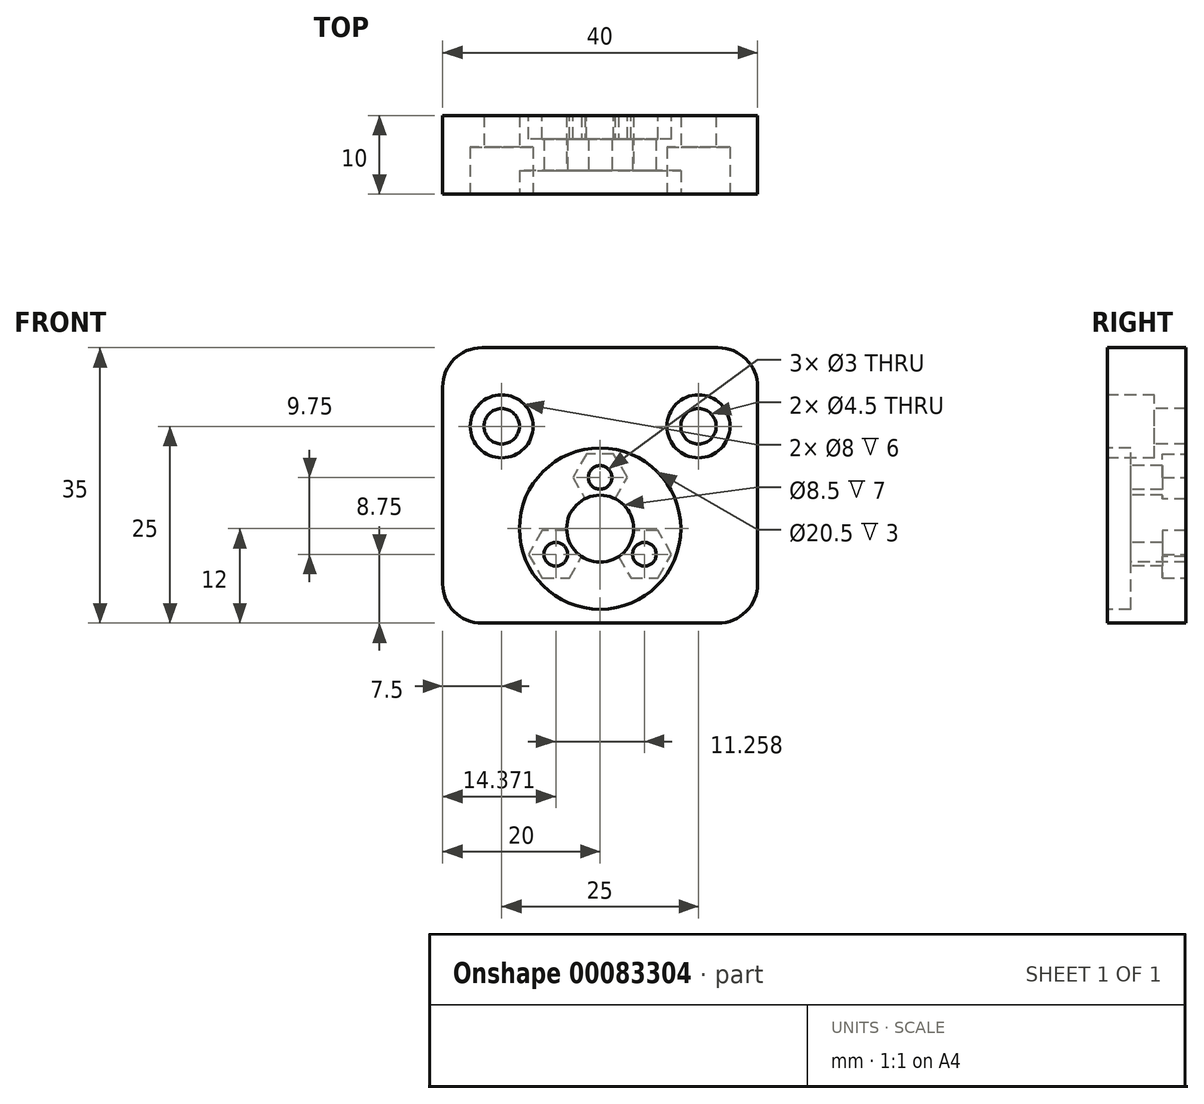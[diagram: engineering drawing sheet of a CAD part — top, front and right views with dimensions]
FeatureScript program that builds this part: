
annotation { "Feature Type Name" : "Feature", "Feature Type Description" : "" }
export const myFeature = defineFeature(function(context is Context, id is Id, definition is map)
    precondition{}
    {
        {
            var Q0;
            Q0=qCreatedBy(makeId("Front.planeOp"),FACE);
            var sketch = newSketch(context, id + "F0", { "sketchPlane" : qUnion([Q0])});
            skLineSegment(sketch, "E0.bottom", {"start": v(-20, -12) * mm, "end": v(20, -12) * mm});
            skLineSegment(sketch, "E0.top", {"start": v(-20, 23) * mm, "end": v(20, 23) * mm});
            skLineSegment(sketch, "E0.left", {"start": v(-20, -12) * mm, "end": v(-20, 23) * mm});
            skLineSegment(sketch, "E0.right", {"start": v(20, -12) * mm, "end": v(20, 23) * mm});
            skCircle(sketch, "E1", {"center": v(0, 0) * mm, "radius": 4.25 * mm});
            skCircle(sketch, "E2.cCircle", {"center": v(0, 0) * mm, "radius": 6.5 * mm, "construction": true});
            skLineSegment(sketch, "E2.0", {"start": v(0, 6.5) * mm, "end": v(5.63, -3.25) * mm, "construction": true});
            skLineSegment(sketch, "E2.1", {"start": v(5.63, -3.25) * mm, "end": v(-5.63, -3.25) * mm, "construction": true});
            skLineSegment(sketch, "E2.2", {"start": v(-5.63, -3.25) * mm, "end": v(0, 6.5) * mm, "construction": true});
            skCircle(sketch, "E3", {"center": v(0, 0) * mm, "radius": 10.25 * mm});
            skCircle(sketch, "E4", {"center": v(0, 6.5) * mm, "radius": 1.5 * mm});
            skCircle(sketch, "E5", {"center": v(5.63, -3.25) * mm, "radius": 1.5 * mm});
            skCircle(sketch, "E6", {"center": v(-5.63, -3.25) * mm, "radius": 1.5 * mm});
            skLineSegment(sketch, "E7", {"start": v(0, -14.58) * mm, "end": v(0, 17.23) * mm, "construction": true});
            skLineSegment(sketch, "E8", {"start": v(-16.58, 0) * mm, "end": v(25.82, 0) * mm, "construction": true});
            skCircle(sketch, "E9", {"center": v(-12.5, 13) * mm, "radius": 2.25 * mm});
            skCircle(sketch, "E10", {"center": v(12.5, 13) * mm, "radius": 2.25 * mm});
            skCircle(sketch, "E11", {"center": v(-12.5, 13) * mm, "radius": 4 * mm});
            skCircle(sketch, "E12", {"center": v(12.5, 13) * mm, "radius": 4 * mm});
            skSolve(sketch);
        }
        {
            var Q0;
            Q0=makeQuery(id+"F0.imprint","IMPRINT",FACE,{"disambiguationData":[TD([[makeQuery(id+"F0.imprint","IMPRINT",EDGE,{"derivedFrom":sQuery(id+"F0.wireOp",EDGE,"E0.bottom")}),1.0]])]});
            var Q1;
            Q1=makeQuery(id+"F0.imprint","IMPRINT",FACE,{"disambiguationData":[TD([[makeQuery(id+"F0.imprint","IMPRINT",EDGE,{"derivedFrom":sQuery(id+"F0.wireOp",EDGE,"E9")}),-1.0]])]});
            var Q2;
            Q2=makeQuery(id+"F0.imprint","IMPRINT",FACE,{"disambiguationData":[TD([[makeQuery(id+"F0.imprint","IMPRINT",EDGE,{"derivedFrom":sQuery(id+"F0.wireOp",EDGE,"E10")}),-1.0]])]});
            var Q3;
            Q3=makeQuery(id+"F0.imprint","IMPRINT",FACE,{"disambiguationData":[TD([[makeQuery(id+"F0.imprint","IMPRINT",EDGE,{"derivedFrom":sQuery(id+"F0.wireOp",EDGE,"E1")}),-1.0]])]});
            extrude(context, id + "F1", {"entities" : qUnion([Q0, Q1, Q2, Q3]), "oppositeDirection" : true, "depth" : 10 * mm});
        }
        {
            var Q0;
            Q0=makeQuery(id+"F0.imprint","IMPRINT",FACE,{"disambiguationData":[TD([[makeQuery(id+"F0.imprint","IMPRINT",EDGE,{"derivedFrom":sQuery(id+"F0.wireOp",EDGE,"E10")}),-1.0]])]});
            var Q1;
            Q1=makeQuery(id+"F0.imprint","IMPRINT",FACE,{"disambiguationData":[TD([[makeQuery(id+"F0.imprint","IMPRINT",EDGE,{"derivedFrom":sQuery(id+"F0.wireOp",EDGE,"E9")}),-1.0]])]});
            extrude(context, id + "F2", {"entities" : qUnion([Q0, Q1]), "operationType" : NewBodyOperationType.REMOVE, "oppositeDirection" : true, "depth" : 6 * mm});
        }
        {
            var Q0;
            Q0=makeQuery(id+"F0.imprint","IMPRINT",FACE,{"disambiguationData":[TD([[makeQuery(id+"F0.imprint","IMPRINT",EDGE,{"derivedFrom":sQuery(id+"F0.wireOp",EDGE,"E1")}),-1.0]])]});
            extrude(context, id + "F3", {"entities" : qUnion([Q0]), "operationType" : NewBodyOperationType.REMOVE, "oppositeDirection" : true, "depth" : 3 * mm});
        }
        {
            var Q0;
            Q0=makeQuery(id+"F1.opExtrude","CAP_FACE",FACE,{"disambiguationData":[OSD([sQuery(id+"F0.wireOp",EDGE,"E0.bottom"),sQuery(id+"F0.wireOp",EDGE,"E0.top"),sQuery(id+"F0.wireOp",EDGE,"E0.left"),sQuery(id+"F0.wireOp",EDGE,"E0.right"),sQuery(id+"F0.wireOp",EDGE,"E1"),sQuery(id+"F0.wireOp",EDGE,"E4"),sQuery(id+"F0.wireOp",EDGE,"E5"),sQuery(id+"F0.wireOp",EDGE,"E6"),sQuery(id+"F0.wireOp",EDGE,"E9"),sQuery(id+"F0.wireOp",EDGE,"E10")])],"isStart":false});
            var sketch = newSketch(context, id + "F4", { "sketchPlane" : qUnion([Q0])});
            skCircle(sketch, "E13", {"center": v(0, 0) * mm, "radius": 3.5 * mm, "construction": true});
            skCircle(sketch, "E14.cCircle", {"center": v(0, 6.5) * mm, "radius": 3 * mm, "construction": true});
            skLineSegment(sketch, "E14.0", {"start": v(-1.73, 9.5) * mm, "end": v(1.73, 9.5) * mm});
            skLineSegment(sketch, "E14.1", {"start": v(1.73, 9.5) * mm, "end": v(3.46, 6.5) * mm});
            skLineSegment(sketch, "E14.2", {"start": v(3.46, 6.5) * mm, "end": v(1.73, 3.5) * mm});
            skLineSegment(sketch, "E14.3", {"start": v(1.73, 3.5) * mm, "end": v(-1.73, 3.5) * mm, "construction": true});
            skLineSegment(sketch, "E14.4", {"start": v(-1.73, 3.5) * mm, "end": v(-3.46, 6.5) * mm});
            skLineSegment(sketch, "E14.5", {"start": v(-3.46, 6.5) * mm, "end": v(-1.73, 9.5) * mm});
            skPoint(sketch, "E14.0.midPoint", {"position": v(0, 9.5) * mm});
            skPoint(sketch, "E15.1.1", {"position": v(-8.23, -4.75) * mm});
            skCircle(sketch, "E15.1.2", {"center": v(-5.63, -3.25) * mm, "radius": 3 * mm, "construction": true});
            skLineSegment(sketch, "E15.1.3", {"start": v(-7.36, -0.25) * mm, "end": v(-3.9, -0.25) * mm});
            skLineSegment(sketch, "E15.1.4", {"start": v(-7.36, -6.25) * mm, "end": v(-9.1, -3.25) * mm});
            skLineSegment(sketch, "E15.1.5", {"start": v(-3.9, -0.25) * mm, "end": v(-2.17, -3.25) * mm, "construction": true});
            skLineSegment(sketch, "E15.1.6", {"start": v(-2.17, -3.25) * mm, "end": v(-3.9, -6.25) * mm});
            skLineSegment(sketch, "E15.1.7", {"start": v(-3.9, -6.25) * mm, "end": v(-7.36, -6.25) * mm});
            skLineSegment(sketch, "E15.1.8", {"start": v(-9.1, -3.25) * mm, "end": v(-7.36, -0.25) * mm});
            skCircle(sketch, "E15.2.0", {"center": v(0, 0) * mm, "radius": 3.5 * mm});
            skPoint(sketch, "E15.2.1", {"position": v(8.23, -4.75) * mm});
            skCircle(sketch, "E15.2.2", {"center": v(5.63, -3.25) * mm, "radius": 3 * mm, "construction": true});
            skLineSegment(sketch, "E15.2.3", {"start": v(3.9, -6.25) * mm, "end": v(2.17, -3.25) * mm});
            skLineSegment(sketch, "E15.2.4", {"start": v(9.1, -3.25) * mm, "end": v(7.36, -6.25) * mm});
            skLineSegment(sketch, "E15.2.5", {"start": v(2.17, -3.25) * mm, "end": v(3.9, -0.25) * mm, "construction": true});
            skLineSegment(sketch, "E15.2.6", {"start": v(3.9, -0.25) * mm, "end": v(7.36, -0.25) * mm});
            skLineSegment(sketch, "E15.2.7", {"start": v(7.36, -0.25) * mm, "end": v(9.1, -3.25) * mm});
            skLineSegment(sketch, "E15.2.8", {"start": v(7.36, -6.25) * mm, "end": v(3.9, -6.25) * mm});
            skLineSegment(sketch, "E16", {"start": v(-1.73, 3.5) * mm, "end": v(-3.9, -0.25) * mm});
            skLineSegment(sketch, "E17", {"start": v(1.73, 3.5) * mm, "end": v(3.9, -0.25) * mm});
            skLineSegment(sketch, "E18", {"start": v(2.17, -3.25) * mm, "end": v(-2.17, -3.25) * mm});
            skSolve(sketch);
        }
        {
            var Q0;
            Q0 = qSketchRegion(id + "F4", true);
            extrude(context, id + "F5", {"entities" : qUnion([Q0]), "operationType" : NewBodyOperationType.REMOVE, "oppositeDirection" : true, "depth" : 3 * mm});
        }
        {
            var Q0;
            Q0=makeQuery(id+"F1.opExtrude","SWEPT_EDGE",EDGE,{"disambiguationData":[OSD([sQuery(id+"F0.wireOp",EDGE,"E0.top"),sQuery(id+"F0.wireOp",EDGE,"E0.left")])]});
            var Q1;
            Q1=makeQuery(id+"F1.opExtrude","SWEPT_EDGE",EDGE,{"disambiguationData":[OSD([sQuery(id+"F0.wireOp",EDGE,"E0.top"),sQuery(id+"F0.wireOp",EDGE,"E0.right")])]});
            var Q2;
            Q2=makeQuery(id+"F1.opExtrude","SWEPT_EDGE",EDGE,{"disambiguationData":[OSD([sQuery(id+"F0.wireOp",EDGE,"E0.bottom"),sQuery(id+"F0.wireOp",EDGE,"E0.right")])]});
            var Q3;
            Q3=makeQuery(id+"F1.opExtrude","SWEPT_EDGE",EDGE,{"disambiguationData":[OSD([sQuery(id+"F0.wireOp",EDGE,"E0.bottom"),sQuery(id+"F0.wireOp",EDGE,"E0.left")])]});
            fillet(context, id + "F6", {"entities" : qUnion([Q0, Q1, Q2, Q3]), "radius" : 5 * mm, "tangentPropagation" : true, "allowEdgeOverflow" : false});
        }
    });
